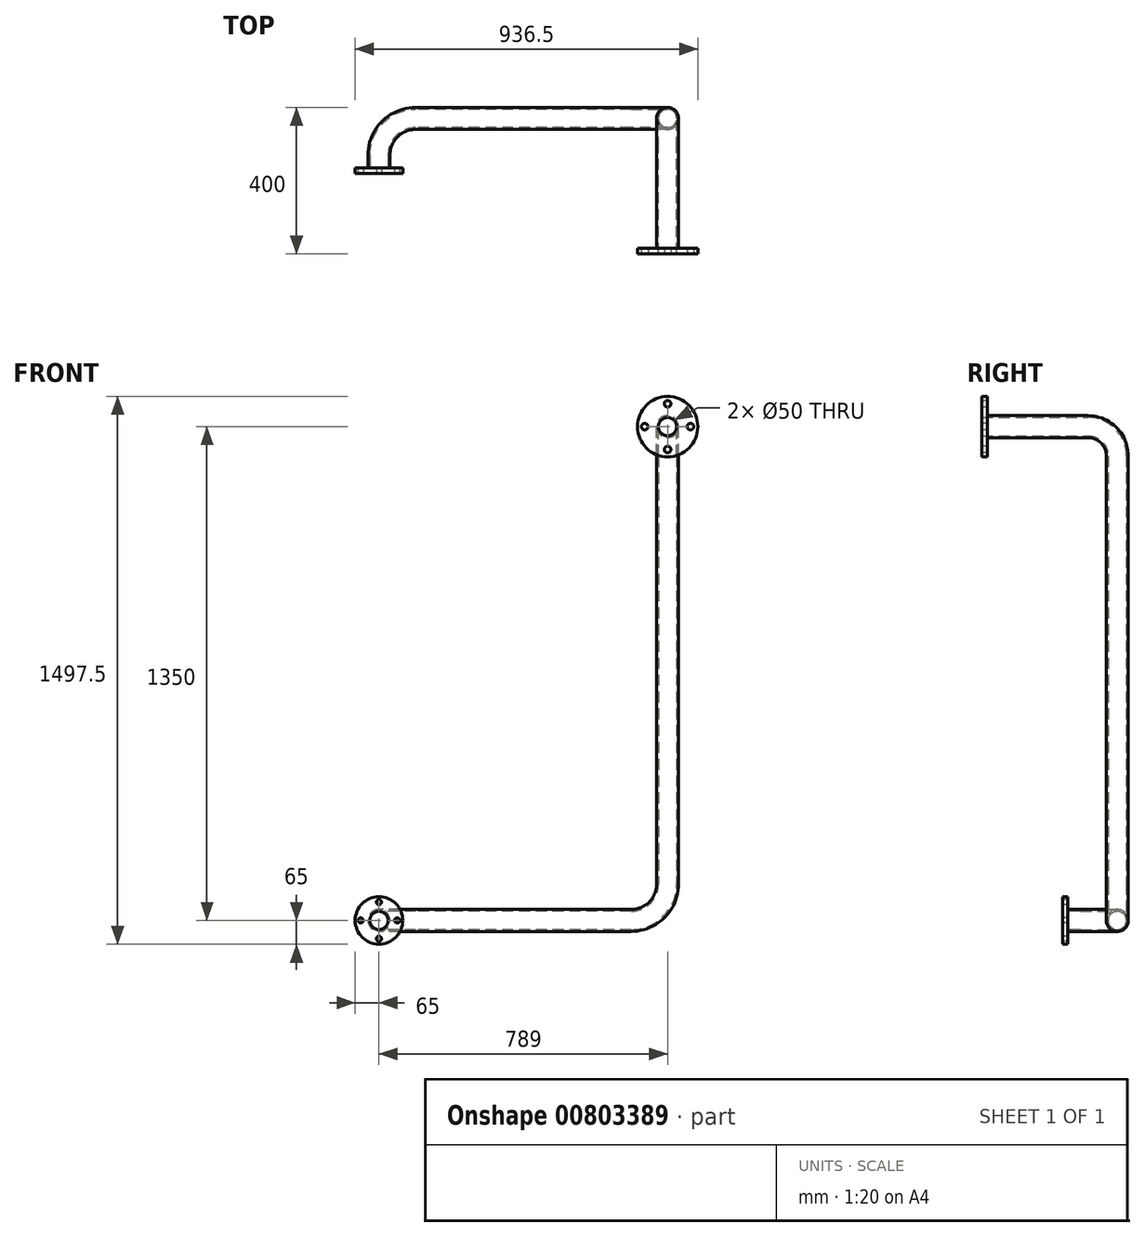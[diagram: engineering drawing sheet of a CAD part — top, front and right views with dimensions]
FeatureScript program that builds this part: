
annotation { "Feature Type Name" : "Feature", "Feature Type Description" : "" }
export const myFeature = defineFeature(function(context is Context, id is Id, definition is map)
    precondition{}
    {
        {
            var Q0;
            Q0=qCreatedBy(makeId("Top.planeOp"),FACE);
            cPlane(context, id + "F0", {"entities" : qUnion([Q0]), "cplaneType" : CPlaneType.OFFSET, "offset" : 1350 * mm, "oppositeDirection" : true, "width" : 150 * mm, "height" : 150 * mm});
        }
        {
            var Q0;
            Q0=qCreatedBy(makeId("Right.planeOp"),FACE);
            var sketch = newSketch(context, id + "F1", { "sketchPlane" : qUnion([Q0])});
            skLineSegment(sketch, "E0", {"start": v(0, 0) * mm, "end": v(290, 0) * mm});
            skLineSegment(sketch, "E1", {"start": v(370, -80) * mm, "end": v(370, -1350) * mm});
            skPoint(sketch, "E2.visualSharp", {"position": v(370, 0) * mm});
            skArc(sketch, "E2.filletArc", {"start": v(370, -80) * mm, "mid": v(346.57, -23.43) * mm, "end": v(290, 0) * mm});
            skLineSegment(sketch, "E3", {"start": v(370, 0) * mm, "end": v(290, 0) * mm});
            skSolve(sketch);
        }
        {
            var Q0;
            Q0=qCreatedBy(makeId("Front.planeOp"),FACE);
            var sketch = newSketch(context, id + "F2", { "sketchPlane" : qUnion([Q0])});
            skCircle(sketch, "E4", {"center": v(0, 0) * mm, "radius": 25 * mm});
            skCircle(sketch, "E5", {"center": v(0, 0) * mm, "radius": 82.5 * mm});
            skCircle(sketch, "E6", {"center": v(0, 62.5) * mm, "radius": 9 * mm});
            skCircle(sketch, "E7.1.0", {"center": v(-62.5, 0) * mm, "radius": 9 * mm});
            skCircle(sketch, "E7.2.0", {"center": v(0, -62.5) * mm, "radius": 9 * mm});
            skCircle(sketch, "E7.3.0", {"center": v(62.5, 0) * mm, "radius": 9 * mm});
            skCircle(sketch, "E8", {"center": v(0, 0) * mm, "radius": 30 * mm});
            skSolve(sketch);
        }
        {
            var Q0;
            Q0=qCreatedBy(makeId("Front.planeOp"),FACE);
            cPlane(context, id + "F3", {"entities" : qUnion([Q0]), "cplaneType" : CPlaneType.OFFSET, "offset" : 370 * mm, "oppositeDirection" : true, "width" : 150 * mm, "height" : 150 * mm});
        }
        {
            var Q0;
            Q0=qCreatedBy(id+"F0.planeOp",FACE);
            var sketch = newSketch(context, id + "F4", { "sketchPlane" : qUnion([Q0])});
            skLineSegment(sketch, "E9.0", {"start": v(-100, 370) * mm, "end": v(-689, 370) * mm});
            skLineSegment(sketch, "E10", {"start": v(-789, 270) * mm, "end": v(-789, 220) * mm});
            skArc(sketch, "E11.filletArc", {"start": v(-689, 370) * mm, "mid": v(-759.71, 340.71) * mm, "end": v(-789, 270) * mm});
            skSolve(sketch);
        }
        {
            var Q0;
            Q0=qCreatedBy(id+"F3.planeOp",FACE);
            var sketch = newSketch(context, id + "F5", { "sketchPlane" : qUnion([Q0])});
            skLineSegment(sketch, "E12.0", {"start": v(0, -80) * mm, "end": v(0, -1250) * mm});
            skPoint(sketch, "E13.visualSharp", {"position": v(0, -1350) * mm});
            skArc(sketch, "E14.MirrorCS", {"start": v(0, -1250) * mm, "mid": v(-29.29, -1320.71) * mm, "end": v(-100, -1350) * mm});
            skPoint(sketch, "E15.filletArc.end.orphan", {"position": v(100, -1350) * mm});
            skPoint(sketch, "E16.MirrorCS.end.orphan", {"position": v(0, -1250) * mm});
            skPoint(sketch, "E17.MirrorCS.end.orphan", {"position": v(-589, -1350) * mm});
            skLineSegment(sketch, "E18", {"start": v(0, 0) * mm, "end": v(-499.18, 0) * mm});
            skLineSegment(sketch, "E19", {"start": v(-599.18, -100.81) * mm, "end": v(-589, -1350) * mm});
            skPoint(sketch, "E20.visualSharp", {"position": v(-600, 0) * mm});
            skArc(sketch, "E20.filletArc", {"start": v(-499.18, 0) * mm, "mid": v(-570.18, -29.58) * mm, "end": v(-599.18, -100.81) * mm});
            skLineSegment(sketch, "E21", {"start": v(-589, -1350) * mm, "end": v(-689, -1350.81) * mm});
            skSolve(sketch);
        }
        {
            var Q0;
            Q0=makeQuery(id+"F2.imprint","IMPRINT",FACE,{"disambiguationData":[TD([[makeQuery(id+"F2.imprint","IMPRINT",EDGE,{"derivedFrom":sQuery(id+"F2.wireOp",EDGE,"E4")}),-1.0]])]});
            var Q1;
            Q1=sQuery(id+"F1.wireOp",EDGE,"E0");
            var Q2;
            Q2=sQuery(id+"F1.wireOp",EDGE,"E2.filletArc");
            var Q3;
            Q3=sQuery(id+"F5.wireOp",EDGE,"E12.0");
            var Q4;
            Q4=sQuery(id+"F5.wireOp",EDGE,"E13.filletArc");
            var Q5;
            Q5=sQuery(id+"F5.wireOp",EDGE,"xq2hsqok-lI8n-Ju7y-0XoG-Kg1ScCQCN3vT");
            var Q6;
            Q6=sQuery(id+"F5.wireOp",EDGE,"1df2cb34-3373-4194-89f4-0ec0ee6fe8e8.filletArc");
            var Q7;
            Q7=sQuery(id+"F5.wireOp",EDGE,"aJzGuewU-24pN-HVPd-WtFy-Gv1arIgnPItI");
            var Q8;
            Q8=sQuery(id+"F5.wireOp",EDGE,"E15.filletArc");
            var Q9;
            Q9=sQuery(id+"F5.wireOp",EDGE,"ualJdYeX-snVT-LolL-3S5l-1RoKmoNRnJfK");
            var Q10;
            Q10=sQuery(id+"F5.wireOp",EDGE,"E14.MirrorCS");
            var Q11;
            Q11=sQuery(id+"F5.wireOp",EDGE,"E17.MirrorCS");
            var Q12;
            Q12=sQuery(id+"F4.wireOp",EDGE,"E9.0");
            var Q13;
            Q13=sQuery(id+"F4.wireOp",EDGE,"E11.filletArc");
            var Q14;
            Q14=sQuery(id+"F4.wireOp",EDGE,"E10");
            sweep(context, id + "F6", {"profiles" : qUnion([Q0]), "path" : qUnion([Q1, Q2, Q3, Q4, Q5, Q6, Q7, Q8, Q9, Q10, Q11, Q12, Q13, Q14])});
        }
        {
            var Q0;
            Q0=makeQuery(id+"F2.imprint","IMPRINT",FACE,{"disambiguationData":[TD([[makeQuery(id+"F2.imprint","IMPRINT",EDGE,{"derivedFrom":sQuery(id+"F2.wireOp",EDGE,"E5")}),1.0]])]});
            extrude(context, id + "F7", {"entities" : qUnion([Q0]), "operationType" : NewBodyOperationType.ADD, "oppositeDirection" : true, "depth" : 15 * mm, "offsetDistance" : 25 * mm});
        }
        {
            var Q0;
            Q0=makeQuery(id+"F6.opSweep","CAP_FACE",FACE,{"disambiguationData":[OSD([sQuery(id+"F2.wireOp",EDGE,"E4"),sQuery(id+"F2.wireOp",EDGE,"E8"),sQuery(id+"F5.wireOp",VERTEX,"aJzGuewU-24pN-HVPd-WtFy-Gv1arIgnPItI.start")])],"isStart":false});
            var sketch = newSketch(context, id + "F8", { "sketchPlane" : qUnion([Q0])});
            skCircle(sketch, "E22", {"center": v(-789, -1350) * mm, "radius": 65 * mm});
            skCircle(sketch, "E23", {"center": v(-789, -1300) * mm, "radius": 7 * mm});
            skCircle(sketch, "E24.1.0", {"center": v(-839, -1350) * mm, "radius": 7 * mm});
            skCircle(sketch, "E24.2.0", {"center": v(-789, -1400) * mm, "radius": 7 * mm});
            skCircle(sketch, "E24.3.0", {"center": v(-739, -1350) * mm, "radius": 7 * mm});
            skSolve(sketch);
        }
        {
            var Q0;
            Q0=makeQuery(id+"F8.imprint","IMPRINT",FACE,{"disambiguationData":[TD([[makeQuery(id+"F8.imprint","IMPRINT",EDGE,{"derivedFrom":sQuery(id+"F8.wireOp",EDGE,"E22")}),1.0]])]});
            extrude(context, id + "F9", {"entities" : qUnion([Q0]), "operationType" : NewBodyOperationType.ADD, "oppositeDirection" : true, "depth" : 15 * mm, "offsetDistance" : 25 * mm});
        }
    });
